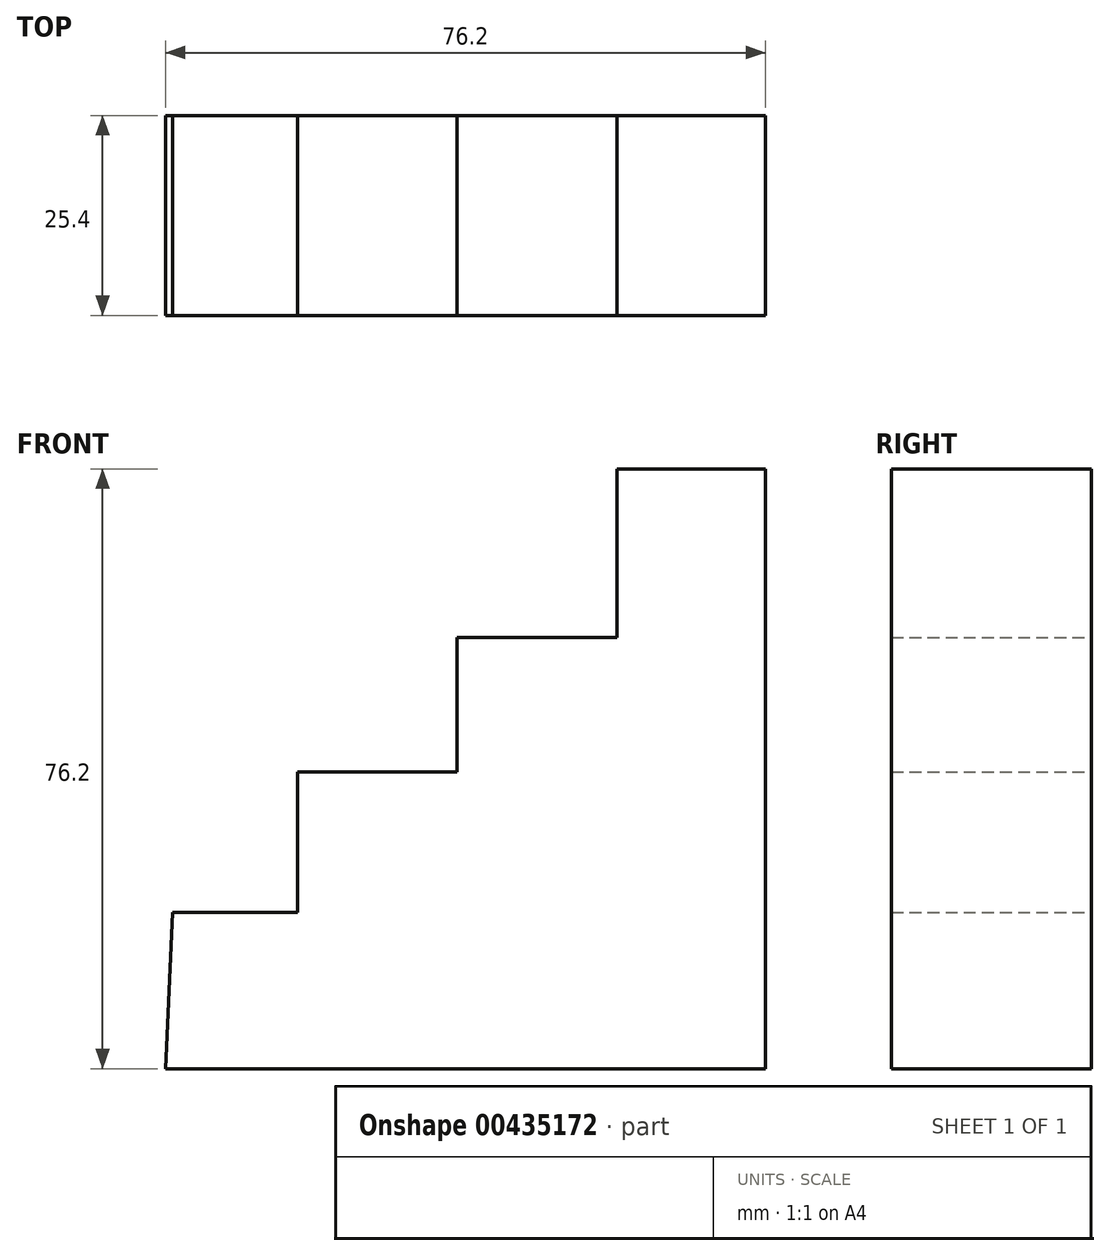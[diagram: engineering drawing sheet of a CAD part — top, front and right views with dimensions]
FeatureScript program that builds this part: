
annotation { "Feature Type Name" : "Feature", "Feature Type Description" : "" }
export const myFeature = defineFeature(function(context is Context, id is Id, definition is map)
    precondition{}
    {
        {
            var Q0;
            Q0=qCreatedBy(makeId("Front.planeOp"),FACE);
            var sketch = newSketch(context, id + "F0", { "sketchPlane" : qUnion([Q0])});
            skLineSegment(sketch, "E0", {"start": v(14.52, 52.52) * mm, "end": v(14.52, -23.68) * mm});
            skLineSegment(sketch, "E1", {"start": v(14.52, -23.68) * mm, "end": v(-61.68, -23.68) * mm});
            skLineSegment(sketch, "E2", {"start": v(14.52, 52.52) * mm, "end": v(-4.37, 52.52) * mm});
            skLineSegment(sketch, "E3", {"start": v(-4.37, 52.52) * mm, "end": v(-4.37, 31.12) * mm});
            skLineSegment(sketch, "E4", {"start": v(-4.37, 31.12) * mm, "end": v(-24.64, 31.12) * mm});
            skLineSegment(sketch, "E5", {"start": v(-24.64, 31.12) * mm, "end": v(-24.64, 14.04) * mm});
            skLineSegment(sketch, "E6", {"start": v(-24.64, 14.04) * mm, "end": v(-44.9, 14.04) * mm});
            skLineSegment(sketch, "E7", {"start": v(-44.9, 14.04) * mm, "end": v(-44.9, -3.85) * mm});
            skLineSegment(sketch, "E8", {"start": v(-44.9, -3.85) * mm, "end": v(-60.8, -3.85) * mm});
            skLineSegment(sketch, "E9", {"start": v(-60.8, -3.85) * mm, "end": v(-61.68, -23.68) * mm});
            skSolve(sketch);
        }
        {
            var Q0;
            Q0 = qSketchRegion(id + "F0", true);
            extrude(context, id + "F1", {"entities" : qUnion([Q0]), "depth" : 25.4 * mm});
        }
    });
